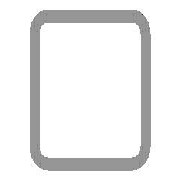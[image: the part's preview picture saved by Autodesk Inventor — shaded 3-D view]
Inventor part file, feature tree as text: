
AUTODESK INVENTOR PART (.ipt)
format: ipt  version: 2025.3 (Build 293356030, 356C)  size: 149,504 bytes
history: native  units: mm (DEFAULTED — no unit token found)
features: other x4, plane x3, split x2, sketch x1
ambient origin geometry x8: Origin, YZ Plane, XZ Plane, XY Plane, X Axis, Y Axis, Z Axis, Center Point
bodies: Solid1 (feature_tree), Body (feature_tree)
feature tree (10):
  parser-record x1  (decoder bookkeeping rows leaked as tree rows — omitted from the tree; the rows remain in map.json)
  other  "Driven Length"
  other  "Start plane"
  other  "End plane"
  plane  "Work Plane4"
  split  "Split1"
  plane  "Work Plane5"
  split  "Split2"
  sketch  "Sketch3"  dims[d3=707.106781mm d4=0.0mm d7=6.0mm d9=60.0mm d11=60.0mm d12=3.0mm d13=-0.0mm d14=707.106781mm d15=30.0mm d16=30.0mm d17=90.0deg d18=707.106781mm]
  plane  "Work Plane3"
